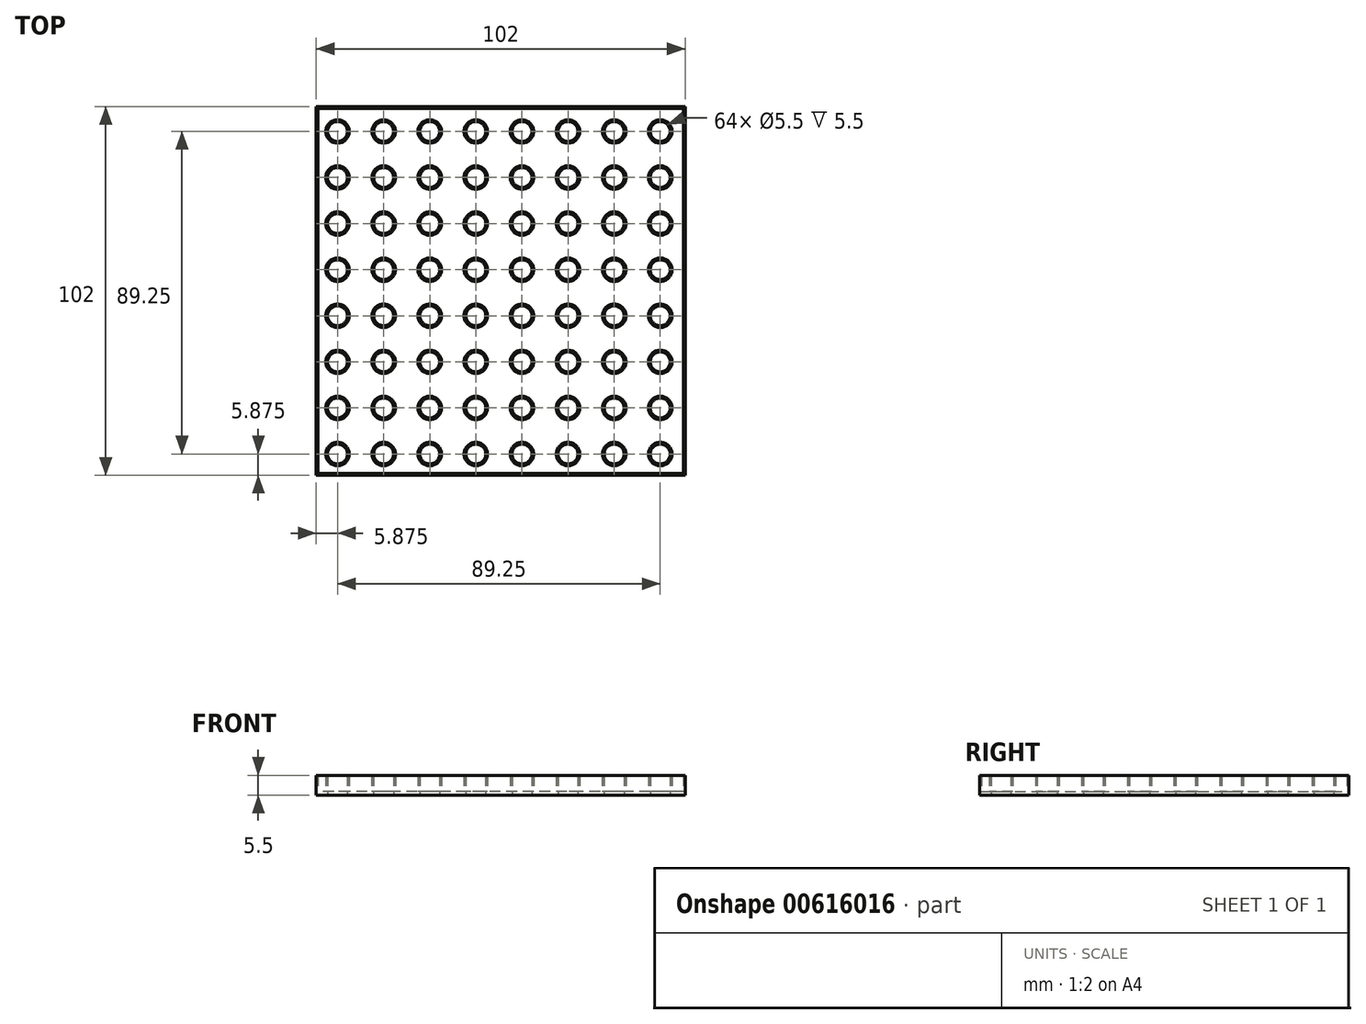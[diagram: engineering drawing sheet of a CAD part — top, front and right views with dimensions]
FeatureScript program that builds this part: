
annotation { "Feature Type Name" : "Feature", "Feature Type Description" : "" }
export const myFeature = defineFeature(function(context is Context, id is Id, definition is map)
    precondition{}
    {
        {
            var Q0;
            Q0=qCreatedBy(makeId("Top.planeOp"),FACE);
            var sketch = newSketch(context, id + "F0", { "sketchPlane" : qUnion([Q0])});
            skLineSegment(sketch, "E0.bottom", {"start": v(51, -51) * mm, "end": v(-51, -51) * mm});
            skLineSegment(sketch, "E0.top", {"start": v(51, 51) * mm, "end": v(-51, 51) * mm});
            skLineSegment(sketch, "E0.left", {"start": v(51, -51) * mm, "end": v(51, 51) * mm});
            skLineSegment(sketch, "E0.right", {"start": v(-51, -51) * mm, "end": v(-51, 51) * mm});
            skPoint(sketch, "E0.middle", {"position": v(0, 0) * mm});
            skCircle(sketch, "E1", {"center": v(-45.13, -45.12) * mm, "radius": 2.75 * mm});
            skCircle(sketch, "E2.0.1.0", {"center": v(-45.13, -32.37) * mm, "radius": 2.75 * mm});
            skCircle(sketch, "E2.0.2.0", {"center": v(-45.13, -19.62) * mm, "radius": 2.75 * mm});
            skCircle(sketch, "E2.0.3.0", {"center": v(-45.13, -6.87) * mm, "radius": 2.75 * mm});
            skCircle(sketch, "E2.0.4.0", {"center": v(-45.13, 5.88) * mm, "radius": 2.75 * mm});
            skCircle(sketch, "E2.0.5.0", {"center": v(-45.13, 18.63) * mm, "radius": 2.75 * mm});
            skCircle(sketch, "E2.0.6.0", {"center": v(-45.13, 31.38) * mm, "radius": 2.75 * mm});
            skCircle(sketch, "E2.0.7.0", {"center": v(-45.13, 44.13) * mm, "radius": 2.75 * mm});
            skCircle(sketch, "E2.1.0.0", {"center": v(-32.38, -45.12) * mm, "radius": 2.75 * mm});
            skCircle(sketch, "E2.1.1.0", {"center": v(-32.38, -32.37) * mm, "radius": 2.75 * mm});
            skCircle(sketch, "E2.1.2.0", {"center": v(-32.38, -19.62) * mm, "radius": 2.75 * mm});
            skCircle(sketch, "E2.1.3.0", {"center": v(-32.38, -6.87) * mm, "radius": 2.75 * mm});
            skCircle(sketch, "E2.1.4.0", {"center": v(-32.38, 5.88) * mm, "radius": 2.75 * mm});
            skCircle(sketch, "E2.1.5.0", {"center": v(-32.38, 18.63) * mm, "radius": 2.75 * mm});
            skCircle(sketch, "E2.1.6.0", {"center": v(-32.38, 31.38) * mm, "radius": 2.75 * mm});
            skCircle(sketch, "E2.1.7.0", {"center": v(-32.38, 44.13) * mm, "radius": 2.75 * mm});
            skCircle(sketch, "E2.2.0.0", {"center": v(-19.62, -45.12) * mm, "radius": 2.75 * mm});
            skCircle(sketch, "E2.2.1.0", {"center": v(-19.62, -32.37) * mm, "radius": 2.75 * mm});
            skCircle(sketch, "E2.2.2.0", {"center": v(-19.62, -19.62) * mm, "radius": 2.75 * mm});
            skCircle(sketch, "E2.2.3.0", {"center": v(-19.62, -6.87) * mm, "radius": 2.75 * mm});
            skCircle(sketch, "E2.2.4.0", {"center": v(-19.62, 5.88) * mm, "radius": 2.75 * mm});
            skCircle(sketch, "E2.2.5.0", {"center": v(-19.62, 18.63) * mm, "radius": 2.75 * mm});
            skCircle(sketch, "E2.2.6.0", {"center": v(-19.62, 31.38) * mm, "radius": 2.75 * mm});
            skCircle(sketch, "E2.2.7.0", {"center": v(-19.62, 44.13) * mm, "radius": 2.75 * mm});
            skCircle(sketch, "E2.3.0.0", {"center": v(-6.87, -45.12) * mm, "radius": 2.75 * mm});
            skCircle(sketch, "E2.3.1.0", {"center": v(-6.87, -32.37) * mm, "radius": 2.75 * mm});
            skCircle(sketch, "E2.3.2.0", {"center": v(-6.87, -19.62) * mm, "radius": 2.75 * mm});
            skCircle(sketch, "E2.3.3.0", {"center": v(-6.87, -6.87) * mm, "radius": 2.75 * mm});
            skCircle(sketch, "E2.3.4.0", {"center": v(-6.87, 5.88) * mm, "radius": 2.75 * mm});
            skCircle(sketch, "E2.3.5.0", {"center": v(-6.87, 18.63) * mm, "radius": 2.75 * mm});
            skCircle(sketch, "E2.3.6.0", {"center": v(-6.87, 31.38) * mm, "radius": 2.75 * mm});
            skCircle(sketch, "E2.3.7.0", {"center": v(-6.87, 44.13) * mm, "radius": 2.75 * mm});
            skCircle(sketch, "E2.4.0.0", {"center": v(5.88, -45.12) * mm, "radius": 2.75 * mm});
            skCircle(sketch, "E2.4.1.0", {"center": v(5.88, -32.37) * mm, "radius": 2.75 * mm});
            skCircle(sketch, "E2.4.2.0", {"center": v(5.88, -19.62) * mm, "radius": 2.75 * mm});
            skCircle(sketch, "E2.4.3.0", {"center": v(5.88, -6.87) * mm, "radius": 2.75 * mm});
            skCircle(sketch, "E2.4.4.0", {"center": v(5.88, 5.88) * mm, "radius": 2.75 * mm});
            skCircle(sketch, "E2.4.5.0", {"center": v(5.88, 18.63) * mm, "radius": 2.75 * mm});
            skCircle(sketch, "E2.4.6.0", {"center": v(5.88, 31.38) * mm, "radius": 2.75 * mm});
            skCircle(sketch, "E2.4.7.0", {"center": v(5.88, 44.13) * mm, "radius": 2.75 * mm});
            skCircle(sketch, "E2.5.0.0", {"center": v(18.63, -45.12) * mm, "radius": 2.75 * mm});
            skCircle(sketch, "E2.5.1.0", {"center": v(18.63, -32.37) * mm, "radius": 2.75 * mm});
            skCircle(sketch, "E2.5.2.0", {"center": v(18.63, -19.62) * mm, "radius": 2.75 * mm});
            skCircle(sketch, "E2.5.3.0", {"center": v(18.63, -6.87) * mm, "radius": 2.75 * mm});
            skCircle(sketch, "E2.5.4.0", {"center": v(18.63, 5.88) * mm, "radius": 2.75 * mm});
            skCircle(sketch, "E2.5.5.0", {"center": v(18.63, 18.63) * mm, "radius": 2.75 * mm});
            skCircle(sketch, "E2.5.6.0", {"center": v(18.63, 31.38) * mm, "radius": 2.75 * mm});
            skCircle(sketch, "E2.5.7.0", {"center": v(18.63, 44.13) * mm, "radius": 2.75 * mm});
            skCircle(sketch, "E2.6.0.0", {"center": v(31.38, -45.12) * mm, "radius": 2.75 * mm});
            skCircle(sketch, "E2.6.1.0", {"center": v(31.38, -32.37) * mm, "radius": 2.75 * mm});
            skCircle(sketch, "E2.6.2.0", {"center": v(31.38, -19.62) * mm, "radius": 2.75 * mm});
            skCircle(sketch, "E2.6.3.0", {"center": v(31.38, -6.87) * mm, "radius": 2.75 * mm});
            skCircle(sketch, "E2.6.4.0", {"center": v(31.38, 5.88) * mm, "radius": 2.75 * mm});
            skCircle(sketch, "E2.6.5.0", {"center": v(31.38, 18.63) * mm, "radius": 2.75 * mm});
            skCircle(sketch, "E2.6.6.0", {"center": v(31.38, 31.38) * mm, "radius": 2.75 * mm});
            skCircle(sketch, "E2.6.7.0", {"center": v(31.38, 44.13) * mm, "radius": 2.75 * mm});
            skCircle(sketch, "E2.7.0.0", {"center": v(44.13, -45.12) * mm, "radius": 2.75 * mm});
            skCircle(sketch, "E2.7.1.0", {"center": v(44.13, -32.37) * mm, "radius": 2.75 * mm});
            skCircle(sketch, "E2.7.2.0", {"center": v(44.13, -19.62) * mm, "radius": 2.75 * mm});
            skCircle(sketch, "E2.7.3.0", {"center": v(44.13, -6.87) * mm, "radius": 2.75 * mm});
            skCircle(sketch, "E2.7.4.0", {"center": v(44.13, 5.88) * mm, "radius": 2.75 * mm});
            skCircle(sketch, "E2.7.5.0", {"center": v(44.13, 18.63) * mm, "radius": 2.75 * mm});
            skCircle(sketch, "E2.7.6.0", {"center": v(44.13, 31.38) * mm, "radius": 2.75 * mm});
            skCircle(sketch, "E2.7.7.0", {"center": v(44.13, 44.13) * mm, "radius": 2.75 * mm});
            skLineSegment(sketch, "E2.direction1", {"start": v(-45.13, -45.12) * mm, "end": v(-32.38, -45.12) * mm, "construction": true});
            skLineSegment(sketch, "E2.direction2", {"start": v(-45.13, -45.12) * mm, "end": v(-45.13, -32.37) * mm, "construction": true});
            skSolve(sketch);
        }
        {
            var Q0;
            Q0=makeQuery(id+"F0.imprint","IMPRINT",FACE,{"disambiguationData":[TD([[makeQuery(id+"F0.imprint","IMPRINT",EDGE,{"derivedFrom":sQuery(id+"F0.wireOp",EDGE,"E0.bottom")}),-1.0]])]});
            extrude(context, id + "F1", {"entities" : qUnion([Q0]), "depth" : 5 * mm, "offsetDistance" : 25 * mm});
        }
        {
            var Q0;
            Q0=makeQuery(id+"F1.opExtrude","CAP_FACE",FACE,{"disambiguationData":[OSD([sQuery(id+"F0.wireOp",EDGE,"E0.bottom"),sQuery(id+"F0.wireOp",EDGE,"E0.top"),sQuery(id+"F0.wireOp",EDGE,"E0.left"),sQuery(id+"F0.wireOp",EDGE,"E0.right"),sQuery(id+"F0.wireOp",EDGE,"E1"),sQuery(id+"F0.wireOp",EDGE,"E2.0.1.0"),sQuery(id+"F0.wireOp",EDGE,"E2.0.2.0"),sQuery(id+"F0.wireOp",EDGE,"E2.0.3.0"),sQuery(id+"F0.wireOp",EDGE,"E2.0.4.0"),sQuery(id+"F0.wireOp",EDGE,"E2.0.5.0"),sQuery(id+"F0.wireOp",EDGE,"E2.0.6.0"),sQuery(id+"F0.wireOp",EDGE,"E2.0.7.0"),sQuery(id+"F0.wireOp",EDGE,"E2.1.0.0"),sQuery(id+"F0.wireOp",EDGE,"E2.1.1.0"),sQuery(id+"F0.wireOp",EDGE,"E2.1.2.0"),sQuery(id+"F0.wireOp",EDGE,"E2.1.3.0"),sQuery(id+"F0.wireOp",EDGE,"E2.1.4.0"),sQuery(id+"F0.wireOp",EDGE,"E2.1.5.0"),sQuery(id+"F0.wireOp",EDGE,"E2.1.6.0"),sQuery(id+"F0.wireOp",EDGE,"E2.1.7.0"),sQuery(id+"F0.wireOp",EDGE,"E2.2.0.0"),sQuery(id+"F0.wireOp",EDGE,"E2.2.1.0"),sQuery(id+"F0.wireOp",EDGE,"E2.2.2.0"),sQuery(id+"F0.wireOp",EDGE,"E2.2.3.0"),sQuery(id+"F0.wireOp",EDGE,"E2.2.4.0"),sQuery(id+"F0.wireOp",EDGE,"E2.2.5.0"),sQuery(id+"F0.wireOp",EDGE,"E2.2.6.0"),sQuery(id+"F0.wireOp",EDGE,"E2.2.7.0"),sQuery(id+"F0.wireOp",EDGE,"E2.3.0.0"),sQuery(id+"F0.wireOp",EDGE,"E2.3.1.0"),sQuery(id+"F0.wireOp",EDGE,"E2.3.2.0"),sQuery(id+"F0.wireOp",EDGE,"E2.3.3.0"),sQuery(id+"F0.wireOp",EDGE,"E2.3.4.0"),sQuery(id+"F0.wireOp",EDGE,"E2.3.5.0"),sQuery(id+"F0.wireOp",EDGE,"E2.3.6.0"),sQuery(id+"F0.wireOp",EDGE,"E2.3.7.0"),sQuery(id+"F0.wireOp",EDGE,"E2.4.0.0"),sQuery(id+"F0.wireOp",EDGE,"E2.4.1.0"),sQuery(id+"F0.wireOp",EDGE,"E2.4.2.0"),sQuery(id+"F0.wireOp",EDGE,"E2.4.3.0"),sQuery(id+"F0.wireOp",EDGE,"E2.4.4.0"),sQuery(id+"F0.wireOp",EDGE,"E2.4.5.0"),sQuery(id+"F0.wireOp",EDGE,"E2.4.6.0"),sQuery(id+"F0.wireOp",EDGE,"E2.4.7.0"),sQuery(id+"F0.wireOp",EDGE,"E2.5.0.0"),sQuery(id+"F0.wireOp",EDGE,"E2.5.1.0"),sQuery(id+"F0.wireOp",EDGE,"E2.5.2.0"),sQuery(id+"F0.wireOp",EDGE,"E2.5.3.0"),sQuery(id+"F0.wireOp",EDGE,"E2.5.4.0"),sQuery(id+"F0.wireOp",EDGE,"E2.5.5.0"),sQuery(id+"F0.wireOp",EDGE,"E2.5.6.0"),sQuery(id+"F0.wireOp",EDGE,"E2.5.7.0"),sQuery(id+"F0.wireOp",EDGE,"E2.6.0.0"),sQuery(id+"F0.wireOp",EDGE,"E2.6.1.0"),sQuery(id+"F0.wireOp",EDGE,"E2.6.2.0"),sQuery(id+"F0.wireOp",EDGE,"E2.6.3.0"),sQuery(id+"F0.wireOp",EDGE,"E2.6.4.0"),sQuery(id+"F0.wireOp",EDGE,"E2.6.5.0"),sQuery(id+"F0.wireOp",EDGE,"E2.6.6.0"),sQuery(id+"F0.wireOp",EDGE,"E2.6.7.0"),sQuery(id+"F0.wireOp",EDGE,"E2.7.0.0"),sQuery(id+"F0.wireOp",EDGE,"E2.7.1.0"),sQuery(id+"F0.wireOp",EDGE,"E2.7.2.0"),sQuery(id+"F0.wireOp",EDGE,"E2.7.3.0"),sQuery(id+"F0.wireOp",EDGE,"E2.7.4.0"),sQuery(id+"F0.wireOp",EDGE,"E2.7.5.0"),sQuery(id+"F0.wireOp",EDGE,"E2.7.6.0"),sQuery(id+"F0.wireOp",EDGE,"E2.7.7.0")])],"isStart":false});
            shell(context, id + "F2", {"entities" : qUnion([Q0]), "thickness" : 0.5 * mm});
        }
        {
            var Q0;
            Q0=makeQuery(id+"F1.opExtrude","CAP_FACE",FACE,{"disambiguationData":[OSD([sQuery(id+"F0.wireOp",EDGE,"E0.bottom"),sQuery(id+"F0.wireOp",EDGE,"E0.top"),sQuery(id+"F0.wireOp",EDGE,"E0.left"),sQuery(id+"F0.wireOp",EDGE,"E0.right"),sQuery(id+"F0.wireOp",EDGE,"E1"),sQuery(id+"F0.wireOp",EDGE,"E2.0.1.0"),sQuery(id+"F0.wireOp",EDGE,"E2.0.2.0"),sQuery(id+"F0.wireOp",EDGE,"E2.0.3.0"),sQuery(id+"F0.wireOp",EDGE,"E2.0.4.0"),sQuery(id+"F0.wireOp",EDGE,"E2.0.5.0"),sQuery(id+"F0.wireOp",EDGE,"E2.0.6.0"),sQuery(id+"F0.wireOp",EDGE,"E2.0.7.0"),sQuery(id+"F0.wireOp",EDGE,"E2.1.0.0"),sQuery(id+"F0.wireOp",EDGE,"E2.1.1.0"),sQuery(id+"F0.wireOp",EDGE,"E2.1.2.0"),sQuery(id+"F0.wireOp",EDGE,"E2.1.3.0"),sQuery(id+"F0.wireOp",EDGE,"E2.1.4.0"),sQuery(id+"F0.wireOp",EDGE,"E2.1.5.0"),sQuery(id+"F0.wireOp",EDGE,"E2.1.6.0"),sQuery(id+"F0.wireOp",EDGE,"E2.1.7.0"),sQuery(id+"F0.wireOp",EDGE,"E2.2.0.0"),sQuery(id+"F0.wireOp",EDGE,"E2.2.1.0"),sQuery(id+"F0.wireOp",EDGE,"E2.2.2.0"),sQuery(id+"F0.wireOp",EDGE,"E2.2.3.0"),sQuery(id+"F0.wireOp",EDGE,"E2.2.4.0"),sQuery(id+"F0.wireOp",EDGE,"E2.2.5.0"),sQuery(id+"F0.wireOp",EDGE,"E2.2.6.0"),sQuery(id+"F0.wireOp",EDGE,"E2.2.7.0"),sQuery(id+"F0.wireOp",EDGE,"E2.3.0.0"),sQuery(id+"F0.wireOp",EDGE,"E2.3.1.0"),sQuery(id+"F0.wireOp",EDGE,"E2.3.2.0"),sQuery(id+"F0.wireOp",EDGE,"E2.3.3.0"),sQuery(id+"F0.wireOp",EDGE,"E2.3.4.0"),sQuery(id+"F0.wireOp",EDGE,"E2.3.5.0"),sQuery(id+"F0.wireOp",EDGE,"E2.3.6.0"),sQuery(id+"F0.wireOp",EDGE,"E2.3.7.0"),sQuery(id+"F0.wireOp",EDGE,"E2.4.0.0"),sQuery(id+"F0.wireOp",EDGE,"E2.4.1.0"),sQuery(id+"F0.wireOp",EDGE,"E2.4.2.0"),sQuery(id+"F0.wireOp",EDGE,"E2.4.3.0"),sQuery(id+"F0.wireOp",EDGE,"E2.4.4.0"),sQuery(id+"F0.wireOp",EDGE,"E2.4.5.0"),sQuery(id+"F0.wireOp",EDGE,"E2.4.6.0"),sQuery(id+"F0.wireOp",EDGE,"E2.4.7.0"),sQuery(id+"F0.wireOp",EDGE,"E2.5.0.0"),sQuery(id+"F0.wireOp",EDGE,"E2.5.1.0"),sQuery(id+"F0.wireOp",EDGE,"E2.5.2.0"),sQuery(id+"F0.wireOp",EDGE,"E2.5.3.0"),sQuery(id+"F0.wireOp",EDGE,"E2.5.4.0"),sQuery(id+"F0.wireOp",EDGE,"E2.5.5.0"),sQuery(id+"F0.wireOp",EDGE,"E2.5.6.0"),sQuery(id+"F0.wireOp",EDGE,"E2.5.7.0"),sQuery(id+"F0.wireOp",EDGE,"E2.6.0.0"),sQuery(id+"F0.wireOp",EDGE,"E2.6.1.0"),sQuery(id+"F0.wireOp",EDGE,"E2.6.2.0"),sQuery(id+"F0.wireOp",EDGE,"E2.6.3.0"),sQuery(id+"F0.wireOp",EDGE,"E2.6.4.0"),sQuery(id+"F0.wireOp",EDGE,"E2.6.5.0"),sQuery(id+"F0.wireOp",EDGE,"E2.6.6.0"),sQuery(id+"F0.wireOp",EDGE,"E2.6.7.0"),sQuery(id+"F0.wireOp",EDGE,"E2.7.0.0"),sQuery(id+"F0.wireOp",EDGE,"E2.7.1.0"),sQuery(id+"F0.wireOp",EDGE,"E2.7.2.0"),sQuery(id+"F0.wireOp",EDGE,"E2.7.3.0"),sQuery(id+"F0.wireOp",EDGE,"E2.7.4.0"),sQuery(id+"F0.wireOp",EDGE,"E2.7.5.0"),sQuery(id+"F0.wireOp",EDGE,"E2.7.6.0"),sQuery(id+"F0.wireOp",EDGE,"E2.7.7.0")])],"isStart":true});
            extrude(context, id + "F3", {"entities" : qUnion([Q0]), "operationType" : NewBodyOperationType.ADD, "depth" : 0.5 * mm, "offsetDistance" : 25 * mm});
        }
    });
